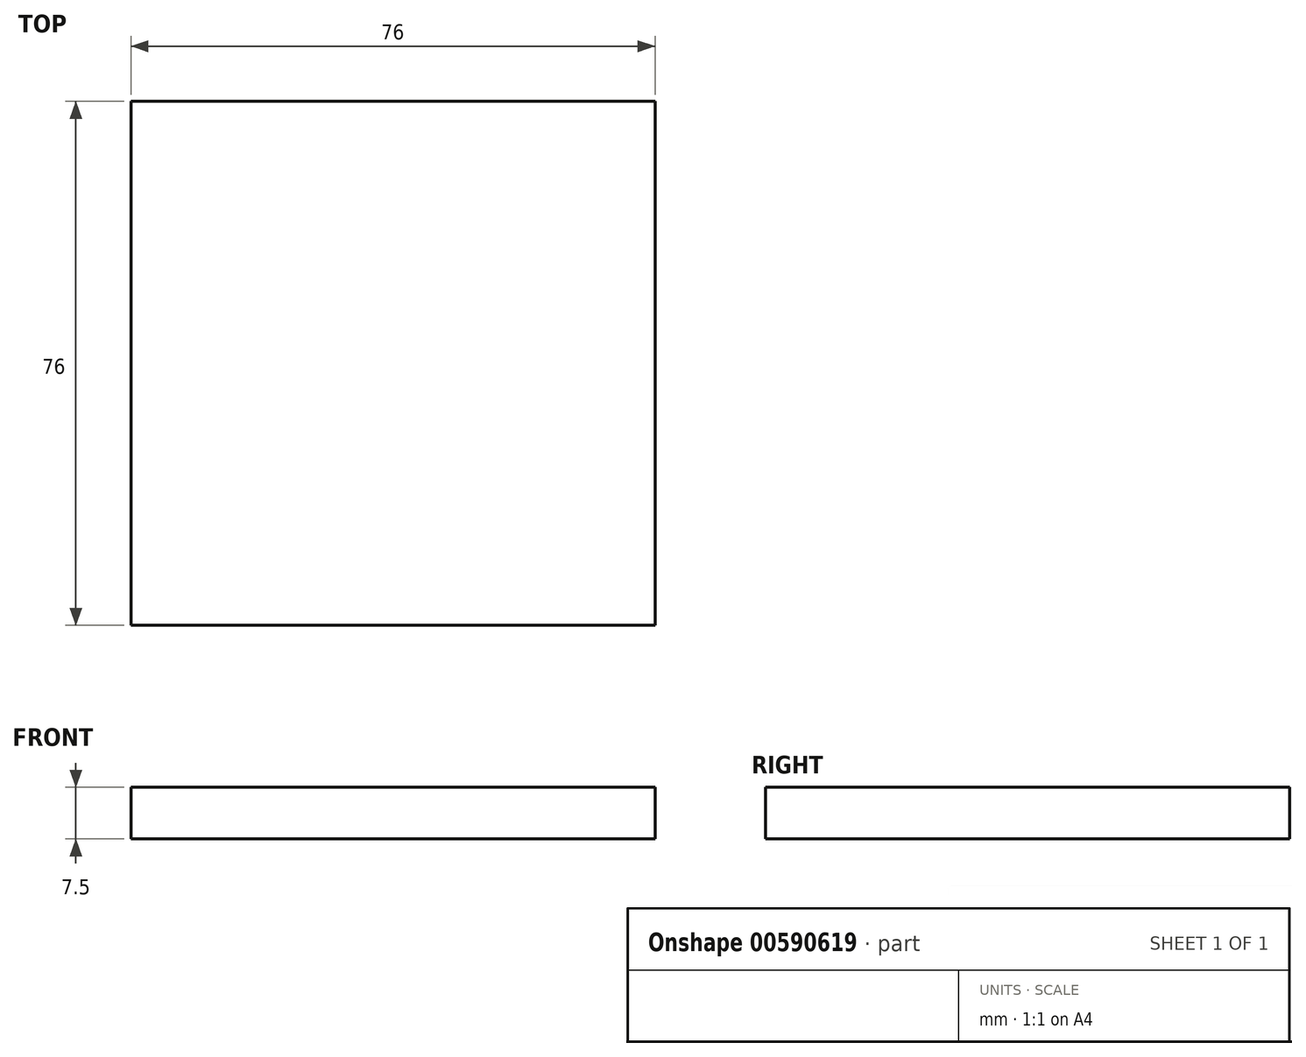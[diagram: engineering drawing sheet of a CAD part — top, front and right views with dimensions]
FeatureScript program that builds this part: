
annotation { "Feature Type Name" : "Feature", "Feature Type Description" : "" }
export const myFeature = defineFeature(function(context is Context, id is Id, definition is map)
    precondition{}
    {
        {
            var Q0;
            Q0=qCreatedBy(makeId("Front.planeOp"),FACE);
            var sketch = newSketch(context, id + "F0", { "sketchPlane" : qUnion([Q0])});
            skLineSegment(sketch, "E0.bottom", {"start": v(0, 0) * mm, "end": v(-76, 0) * mm});
            skLineSegment(sketch, "E0.top", {"start": v(0, 7.5) * mm, "end": v(-76, 7.5) * mm});
            skLineSegment(sketch, "E0.left", {"start": v(0, 0) * mm, "end": v(0, 7.5) * mm});
            skLineSegment(sketch, "E0.right", {"start": v(-76, 0) * mm, "end": v(-76, 7.5) * mm});
            skSolve(sketch);
        }
        {
            var Q0;
            Q0 = qSketchRegion(id + "F0", true);
            extrude(context, id + "F1", {"entities" : qUnion([Q0]), "depth" : 76 * mm, "offsetDistance" : 25 * mm});
        }
    });
